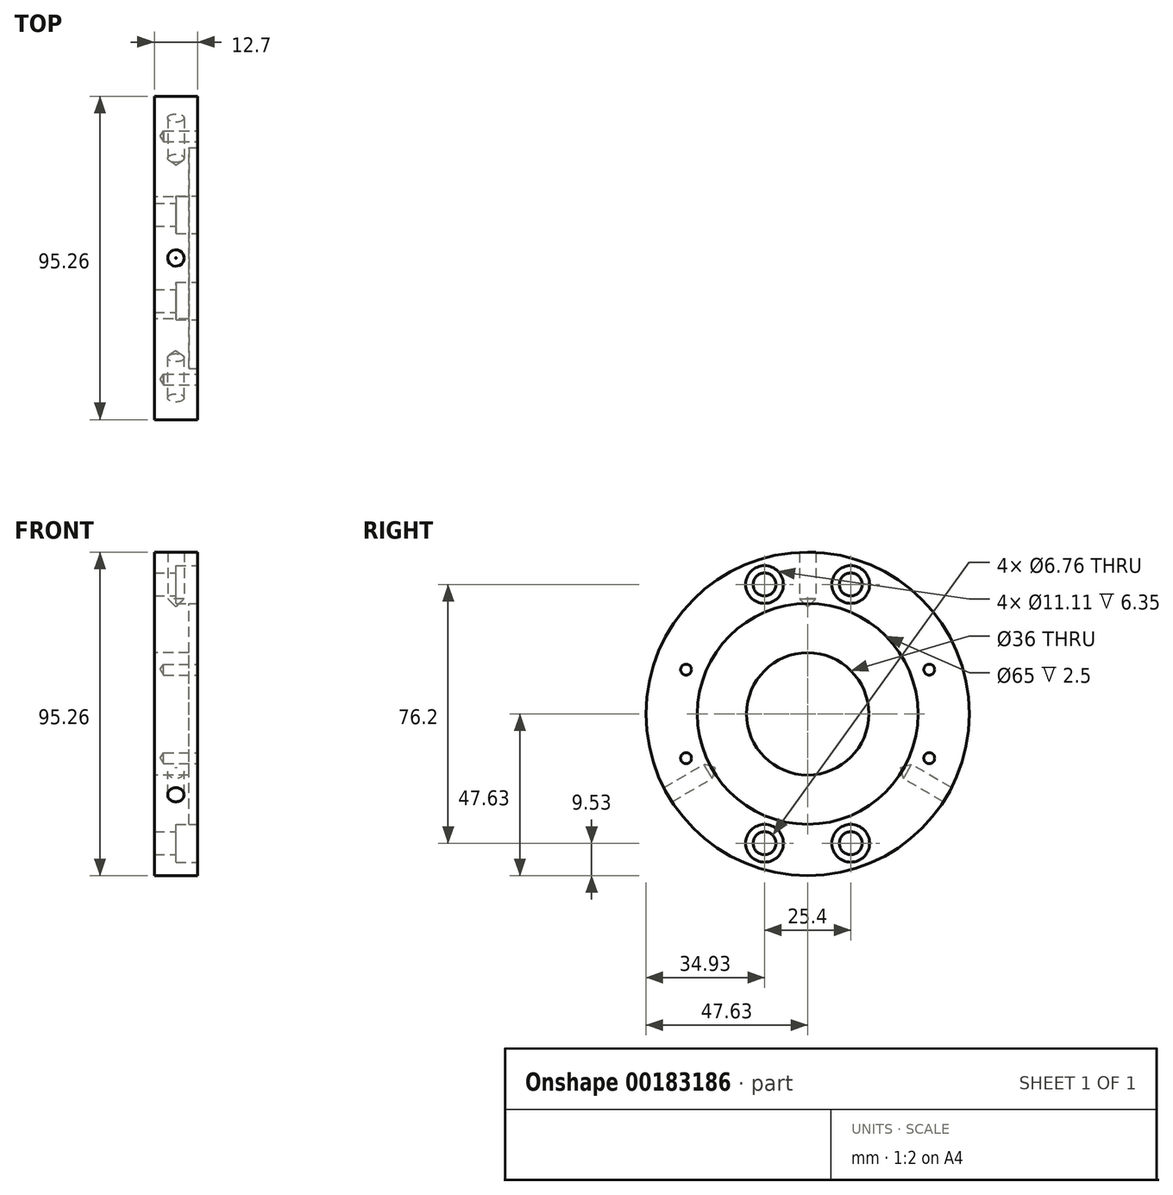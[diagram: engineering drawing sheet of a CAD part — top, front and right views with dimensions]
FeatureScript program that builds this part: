
annotation { "Feature Type Name" : "Feature", "Feature Type Description" : "" }
export const myFeature = defineFeature(function(context is Context, id is Id, definition is map)
    precondition{}
    {
        {
            var Q0;
            Q0=qCreatedBy(makeId("Right.planeOp"),FACE);
            var sketch = newSketch(context, id + "F0", { "sketchPlane" : qUnion([Q0])});
            skCircle(sketch, "E0", {"center": v(0, 0) * mm, "radius": 47.63 * mm});
            skCircle(sketch, "E1", {"center": v(0, 0) * mm, "radius": 18 * mm});
            skSolve(sketch);
        }
        {
            var Q0;
            Q0 = qSketchRegion(id + "F0", true);
            extrude(context, id + "F1", {"entities" : qUnion([Q0]), "endBound" : BoundingType.SYMMETRIC, "depth" : 12.7 * mm});
        }
        {
            var Q0;
            Q0=makeQuery(id+"F1.opExtrude","CAP_FACE",FACE,{"disambiguationData":[OSD([sQuery(id+"F0.wireOp",EDGE,"E0"),sQuery(id+"F0.wireOp",EDGE,"E1")])],"isStart":false});
            var sketch = newSketch(context, id + "F2", { "sketchPlane" : qUnion([Q0])});
            skCircle(sketch, "E2", {"center": v(0, 0) * mm, "radius": 32.5 * mm});
            skSolve(sketch);
        }
        {
            var Q0;
            Q0 = qSketchRegion(id + "F2", true);
            extrude(context, id + "F3", {"entities" : qUnion([Q0]), "operationType" : NewBodyOperationType.REMOVE, "oppositeDirection" : true, "depth" : 2.5 * mm});
        }
        {
            var Q0;
            Q0=makeQuery(id+"F1.opExtrude","CAP_FACE",FACE,{"disambiguationData":[OSD([sQuery(id+"F0.wireOp",EDGE,"E0"),sQuery(id+"F0.wireOp",EDGE,"E1")])],"isStart":false});
            var sketch = newSketch(context, id + "F4", { "sketchPlane" : qUnion([Q0])});
            skLineSegment(sketch, "E3", {"start": v(0, 73.08) * mm, "end": v(0, -81.1) * mm, "construction": true});
            skLineSegment(sketch, "E4", {"start": v(-80.49, 0) * mm, "end": v(82.9, 0) * mm, "construction": true});
            skLineSegment(sketch, "E5.0", {"start": v(-35.81, 73.08) * mm, "end": v(-35.81, -81.1) * mm, "construction": true});
            skCircle(sketch, "E6.0", {"center": v(0, 0) * mm, "radius": 38.85 * mm, "construction": true});
            skLineSegment(sketch, "E7", {"start": v(0, 0) * mm, "end": v(-55.99, 20.38) * mm, "construction": true});
            skPoint(sketch, "E8", {"position": v(-35.81, 13.04) * mm});
            skPoint(sketch, "E9.MirrorP", {"position": v(35.81, 13.04) * mm});
            skPoint(sketch, "E10.MirrorP", {"position": v(35.81, -13.04) * mm});
            skPoint(sketch, "E11.MirrorP", {"position": v(-35.81, -13.04) * mm});
            skSolve(sketch);
        }
        {
            var Q0;
            Q0=sQuery(id+"F4.wireOp",VERTEX,"E8");
            var Q1;
            Q1=sQuery(id+"F4.wireOp",VERTEX,"E9.MirrorP");
            var Q2;
            Q2=sQuery(id+"F4.wireOp",VERTEX,"E10.MirrorP");
            var Q3;
            Q3=sQuery(id+"F4.wireOp",VERTEX,"E11.MirrorP");
            var Q4;
            Q4=makeQuery(id+"F1.opExtrude","SWEPT_BODY",BODY,{"disambiguationData":[OSD([sQuery(id+"F0.wireOp",EDGE,"E0"),sQuery(id+"F0.wireOp",EDGE,"E1")])]});
            hole(context, id + "F5", {"style" : HoleStyle.SIMPLE, "endStyle" : HoleEndStyle.BLIND, "standardTappedOrClearance" : lookupTablePath({ "standard" : "ISO", "engagement" : "75%", "pitch" : "0.75 mm", "size" : "M4", "type" : "Tapped" }), "standardBlindInLast" : lookupTablePath({ "standard" : "ISO", "engagement" : "75%", "pitch" : "0.75 mm", "size" : "M4", "type" : "Tapped" }), "holeDiameter" : 3.2 * mm, "holeDepth" : 10 * mm, "locations" : qUnion([Q0, Q1, Q2, Q3]), "scope" : qUnion([Q4])});
        }
        {
            var Q0;
            Q0=makeQuery(id+"F1.opExtrude","CAP_FACE",FACE,{"disambiguationData":[OSD([sQuery(id+"F0.wireOp",EDGE,"E0"),sQuery(id+"F0.wireOp",EDGE,"E1")])],"isStart":false});
            var sketch = newSketch(context, id + "F6", { "sketchPlane" : qUnion([Q0])});
            skLineSegment(sketch, "E12", {"start": v(-56.7, 0) * mm, "end": v(53.25, 0) * mm, "construction": true});
            skLineSegment(sketch, "E13", {"start": v(0, 60.7) * mm, "end": v(0, -57.38) * mm, "construction": true});
            skLineSegment(sketch, "E14.0", {"start": v(-56.7, 38.1) * mm, "end": v(53.25, 38.1) * mm, "construction": true});
            skLineSegment(sketch, "E15.0", {"start": v(-12.7, 60.7) * mm, "end": v(-12.7, -57.38) * mm, "construction": true});
            skPoint(sketch, "E16", {"position": v(-12.7, 38.1) * mm});
            skPoint(sketch, "E17.MirrorP", {"position": v(12.7, 38.1) * mm});
            skPoint(sketch, "E18.MirrorP", {"position": v(-12.7, -38.1) * mm});
            skPoint(sketch, "E19.MirrorP", {"position": v(12.7, -38.1) * mm});
            skSolve(sketch);
        }
        {
            var Q0;
            Q0=sQuery(id+"F6.wireOp",VERTEX,"E16");
            var Q1;
            Q1=sQuery(id+"F6.wireOp",VERTEX,"E17.MirrorP");
            var Q2;
            Q2=sQuery(id+"F6.wireOp",VERTEX,"E18.MirrorP");
            var Q3;
            Q3=sQuery(id+"F6.wireOp",VERTEX,"E19.MirrorP");
            var Q4;
            Q4=makeQuery(id+"F1.opExtrude","SWEPT_BODY",BODY,{"disambiguationData":[OSD([sQuery(id+"F0.wireOp",EDGE,"E0"),sQuery(id+"F0.wireOp",EDGE,"E1")])]});
            hole(context, id + "F7", {"style" : HoleStyle.C_BORE, "endStyle" : HoleEndStyle.THROUGH, "standardTappedOrClearance" : lookupTablePath({ "standard" : "ANSI", "fit" : "Normal (ASME)", "size" : "1/4", "type" : "Clearance" }), "standardBlindInLast" : lookupTablePath({ "fit" : "Free", "standard" : "ANSI", "size" : "1/4", "type" : "Clearance" }), "holeDiameter" : 6.76 * mm, "cBoreDiameter" : 11.1 * mm, "cBoreDepth" : 6.35 * mm, "locations" : qUnion([Q0, Q1, Q2, Q3]), "scope" : qUnion([Q4]), "isTappedThrough" : true});
        }
        {
            var Q0;
            Q0=qCreatedBy(makeId("Top.planeOp"),FACE);
            cPlane(context, id + "F8", {"entities" : qUnion([Q0]), "cplaneType" : CPlaneType.OFFSET, "offset" : 47.62 * mm, "width" : 152.4 * mm, "height" : 152.4 * mm});
        }
        {
            var Q0;
            Q0=qCreatedBy(id+"F8.planeOp",FACE);
            var sketch = newSketch(context, id + "F9", { "sketchPlane" : qUnion([Q0])});
            skLineSegment(sketch, "E20.0", {"start": v(-6.35, 47.63) * mm, "end": v(-6.35, -47.63) * mm, "construction": true});
            skLineSegment(sketch, "E21.0", {"start": v(6.35, 47.63) * mm, "end": v(6.35, -47.63) * mm, "construction": true});
            skLineSegment(sketch, "E22", {"start": v(-6.35, 0) * mm, "end": v(6.35, 0) * mm, "construction": true});
            skCircle(sketch, "E23", {"center": v(0, 0) * mm, "radius": 2.41 * mm});
            skSolve(sketch);
        }
        {
            var Q0;
            Q0 = qSketchRegion(id + "F9", true);
            extrude(context, id + "F10", {"entities" : qUnion([Q0]), "endBound" : BoundingType.SYMMETRIC, "depth" : 32 * mm});
        }
        {
            var Q0;
            Q0=makeQuery(id+"F10.opExtrude","CAP_EDGE",EDGE,{"disambiguationData":[OSD([sQuery(id+"F9.wireOp",EDGE,"E23")])],"isStart":true});
            chamfer(context, id + "F11", {"entities" : qUnion([Q0]), "width" : 2.3 * mm, "tangentPropagation" : true});
        }
        {
            var Q0;
            Q0=qCreatedBy(makeId("Top.planeOp"),FACE);
            var sketch = newSketch(context, id + "F12", { "sketchPlane" : qUnion([Q0])});
            skLineSegment(sketch, "E24", {"start": v(-91.86, 0) * mm, "end": v(92.25, 0) * mm, "construction": true});
            skSolve(sketch);
        }
        {
            var Q0;
            Q0=makeQuery(id+"F10.opExtrude","SWEPT_BODY",BODY,{"disambiguationData":[OSD([sQuery(id+"F9.wireOp",EDGE,"E23")])]});
            var Q1;
            Q1=sQuery(id+"F12.wireOp",EDGE,"E24");
            circularPattern(context, id + "F13", {"entities" : qUnion([Q0]), "axis" : qUnion([Q1]), "angle" : 120 * degree, "instanceCount" : 3});
        }
        {
            var Q0;
            Q0=makeQuery(id+"F10.opExtrude","SWEPT_BODY",BODY,{"disambiguationData":[OSD([sQuery(id+"F9.wireOp",EDGE,"E23")])]});
            var Q1;
            Q1=makeQuery(id+"F13.opPattern","COPY",BODY,{"derivedFrom":makeQuery(id+"F10.opExtrude","SWEPT_BODY",BODY,{"disambiguationData":[OSD([sQuery(id+"F9.wireOp",EDGE,"E23")])]}),"instanceName":"1"});
            var Q2;
            Q2=makeQuery(id+"F13.opPattern","COPY",BODY,{"derivedFrom":makeQuery(id+"F10.opExtrude","SWEPT_BODY",BODY,{"disambiguationData":[OSD([sQuery(id+"F9.wireOp",EDGE,"E23")])]}),"instanceName":"2"});
            var Q3;
            Q3=makeQuery(id+"F1.opExtrude","SWEPT_BODY",BODY,{"disambiguationData":[OSD([sQuery(id+"F0.wireOp",EDGE,"E0"),sQuery(id+"F0.wireOp",EDGE,"E1")])]});
            booleanBodies(context, id + "F14", {"operationType" : BooleanOperationType.SUBTRACTION, "tools" : qUnion([Q0, Q1, Q2]), "targets" : qUnion([Q3])});
        }
    });
